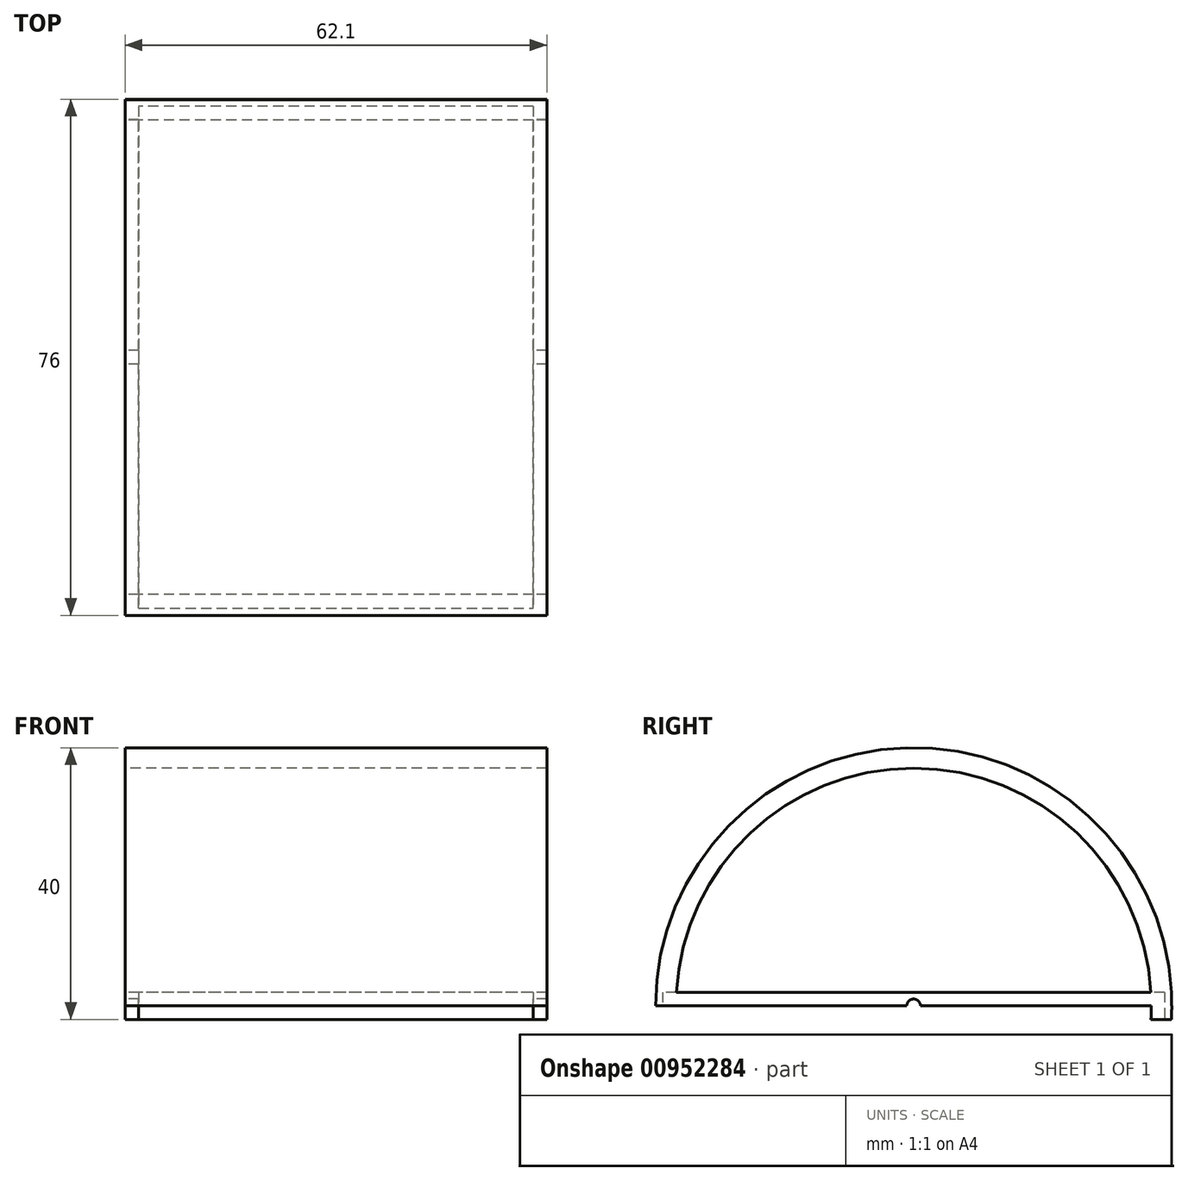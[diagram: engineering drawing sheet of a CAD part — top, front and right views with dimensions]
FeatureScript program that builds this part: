
annotation { "Feature Type Name" : "Feature", "Feature Type Description" : "" }
export const myFeature = defineFeature(function(context is Context, id is Id, definition is map)
    precondition{}
    {
        {
            var Q0;
            Q0=qCreatedBy(makeId("Right.planeOp"),FACE);
            var sketch = newSketch(context, id + "F0", { "sketchPlane" : qUnion([Q0])});
            skCircle(sketch, "E0", {"center": v(0, 0) * mm, "radius": 35 * mm});
            skCircle(sketch, "E1", {"center": v(0, 0) * mm, "radius": 38 * mm});
            skLineSegment(sketch, "E2", {"start": v(-38, 0) * mm, "end": v(38, 0) * mm});
            skLineSegment(sketch, "E3.top", {"start": v(-38, -2) * mm, "end": v(38, -2) * mm});
            skLineSegment(sketch, "E3.left", {"start": v(-38, 0) * mm, "end": v(-38, -2) * mm});
            skLineSegment(sketch, "E3.right", {"start": v(38, 0) * mm, "end": v(38, -2) * mm});
            skLineSegment(sketch, "E4.bottom", {"start": v(-38, 0) * mm, "end": v(37.95, 0) * mm});
            skLineSegment(sketch, "E4.top", {"start": v(-38, 2) * mm, "end": v(37.95, 2) * mm});
            skLineSegment(sketch, "E4.left", {"start": v(-38, 0) * mm, "end": v(-38, 2) * mm});
            skLineSegment(sketch, "E4.right", {"start": v(37.95, 0) * mm, "end": v(37.95, 2) * mm});
            skCircle(sketch, "E5", {"center": v(0, 0) * mm, "radius": 1 * mm});
            skSolve(sketch);
        }
        {
            var Q0;
            {var subQ0=sQuery(id+"F0.wireOp",EDGE,"E4.top");var subQ1=sQuery(id+"F0.wireOp",EDGE,"E0");var subQ2=makeQuery(id+"F0.imprint","INTERSECT",VERTEX,{"disambiguationData":[OD(1.0)],"derivedFrom":[subQ1,subQ0]});Q0=makeQuery(id+"F0.imprint","IMPRINT",FACE,{"disambiguationData":[TD([[makeQuery(id+"F0.imprint","IMPRINT",EDGE,{"disambiguationData":[TD([[subQ2,-1.0]])],"derivedFrom":subQ1}),-1.0]])]});}
            var Q1;
            {var subQ0=sQuery(id+"F0.wireOp",EDGE,"E4.top");var subQ1=sQuery(id+"F0.wireOp",EDGE,"E0");var subQ2=makeQuery(id+"F0.imprint","INTERSECT",VERTEX,{"disambiguationData":[OD(0.0)],"derivedFrom":[subQ1,subQ0]});Q1=makeQuery(id+"F0.imprint","IMPRINT",FACE,{"disambiguationData":[TD([[makeQuery(id+"F0.imprint","IMPRINT",EDGE,{"disambiguationData":[TD([[subQ2,-1.0]])],"derivedFrom":subQ1}),-1.0]])]});}
            var Q2;
            {var subQ1=sQuery(id+"F0.wireOp",EDGE,"E0");var subQ7=sQuery(id+"F0.wireOp",EDGE,"E4.top");var subQ9=makeQuery(id+"F0.imprint","INTERSECT",VERTEX,{"disambiguationData":[OD(0.0)],"derivedFrom":[subQ1,subQ7]});Q2=makeQuery(id+"F0.imprint","IMPRINT",FACE,{"disambiguationData":[TD([[makeQuery(id+"F0.imprint","IMPRINT",EDGE,{"disambiguationData":[TD([[subQ9,1.0]])],"derivedFrom":subQ1}),1.0]])]});}
            var Q3;
            {var subQ0=sQuery(id+"F0.wireOp",EDGE,"E4.bottom");var subQ1=sQuery(id+"F0.wireOp",EDGE,"E0");var subQ2=makeQuery(id+"F0.imprint","INTERSECT",VERTEX,{"disambiguationData":[OD(1.0)],"derivedFrom":[subQ1,subQ0]});Q3=makeQuery(id+"F0.imprint","IMPRINT",FACE,{"disambiguationData":[TD([[makeQuery(id+"F0.imprint","IMPRINT",EDGE,{"disambiguationData":[TD([[subQ2,-1.0]])],"derivedFrom":subQ1}),1.0]])]});}
            var Q4;
            {var subQ0=sQuery(id+"F0.wireOp",EDGE,"E4.bottom");var subQ1=sQuery(id+"F0.wireOp",EDGE,"E0");var subQ2=makeQuery(id+"F0.imprint","INTERSECT",VERTEX,{"disambiguationData":[OD(1.0)],"derivedFrom":[subQ1,subQ0]});Q4=makeQuery(id+"F0.imprint","IMPRINT",FACE,{"disambiguationData":[TD([[makeQuery(id+"F0.imprint","IMPRINT",EDGE,{"disambiguationData":[TD([[subQ2,-1.0]])],"derivedFrom":subQ1}),-1.0]])]});}
            var Q5;
            {var subQ0=sQuery(id+"F0.wireOp",EDGE,"E2");Q5=makeQuery(id+"F0.imprint","IMPRINT",FACE,{"disambiguationData":[TD([[makeQuery(id+"F0.imprint","IMPRINT",EDGE,{"derivedFrom":subQ0}),-1.0]])]});}
            var Q6;
            {var subQ5=sQuery(id+"F0.wireOp",EDGE,"E4.right");Q6=makeQuery(id+"F0.imprint","IMPRINT",FACE,{"disambiguationData":[TD([[makeQuery(id+"F0.imprint","IMPRINT",EDGE,{"derivedFrom":subQ5}),1.0]])]});}
            extrude(context, id + "F1", {"entities" : qUnion([Q0, Q1, Q2, Q3, Q4, Q5, Q6]), "depth" : 62.1 * mm, "offsetDistance" : 25 * mm, "symmetric" : true});
        }
        {
            var Q0;
            Q0=makeQuery(id+"F1.opExtrude","SWEPT_FACE",FACE,{"disambiguationData":[OSD([sQuery(id+"F0.wireOp",EDGE,"E3.top")])]});
            var sketch = newSketch(context, id + "F2", { "sketchPlane" : qUnion([Q0])});
            skLineSegment(sketch, "E6.bottom", {"start": v(29.05, -36.95) * mm, "end": v(-29.05, -36.95) * mm});
            skLineSegment(sketch, "E6.top", {"start": v(29.05, 36.95) * mm, "end": v(-29.05, 36.95) * mm});
            skLineSegment(sketch, "E6.left", {"start": v(29.05, -36.95) * mm, "end": v(29.05, 36.95) * mm});
            skLineSegment(sketch, "E6.right", {"start": v(-29.05, -36.95) * mm, "end": v(-29.05, 36.95) * mm});
            skPoint(sketch, "E6.middle", {"position": v(0, 0) * mm});
            skSolve(sketch);
        }
        {
            var Q0;
            Q0 = qSketchRegion(id + "F2", true);
            var Q1;
            Q1=makeQuery(id+"F1.opExtrude","SWEPT_FACE",FACE,{"disambiguationData":[OSD([sQuery(id+"F0.wireOp",EDGE,"E4.top")])]});
            extrude(context, id + "F3", {"entities" : qUnion([Q0]), "operationType" : NewBodyOperationType.REMOVE, "endBound" : BoundingType.UP_TO_SURFACE, "oppositeDirection" : true, "depth" : 25 * mm, "endBoundEntityFace" : qUnion([Q1]), "offsetDistance" : 25 * mm});
        }
    });
